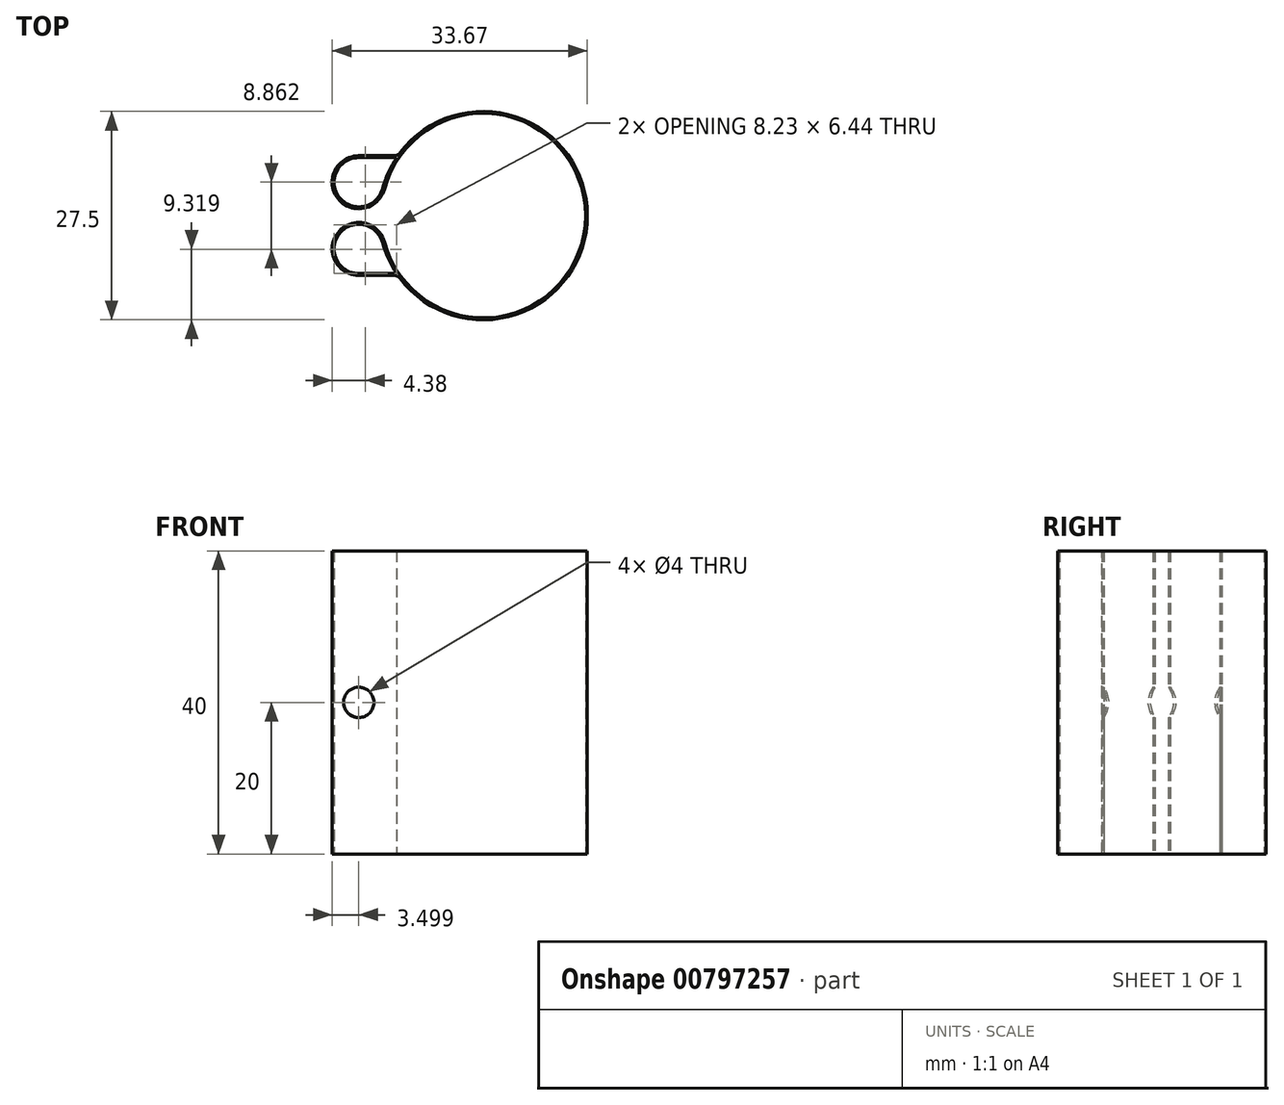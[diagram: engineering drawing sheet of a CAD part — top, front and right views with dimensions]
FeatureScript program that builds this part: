
annotation { "Feature Type Name" : "Feature", "Feature Type Description" : "" }
export const myFeature = defineFeature(function(context is Context, id is Id, definition is map)
    precondition{}
    {
        {
            var Q0;
            Q0=qCreatedBy(makeId("Top.planeOp"),FACE);
            var sketch = newSketch(context, id + "F0", { "sketchPlane" : qUnion([Q0])});
            skArc(sketch, "E0", {"start": v(-13.04, -3.5) * mm, "mid": v(13.5, 0) * mm, "end": v(-13.04, 3.5) * mm});
            skArc(sketch, "E1", {"start": v(-13.28, -3.56) * mm, "mid": v(-12.52, -5.68) * mm, "end": v(-11.43, -7.65) * mm});
            skLineSegment(sketch, "E2", {"start": v(0, 0) * mm, "end": v(13.75, 0) * mm, "construction": true});
            skLineSegment(sketch, "E3.1.0", {"start": v(0, 0) * mm, "end": v(0, 13.75) * mm, "construction": true});
            skLineSegment(sketch, "E3.2.0", {"start": v(0, 0) * mm, "end": v(-13.75, 0) * mm, "construction": true});
            skLineSegment(sketch, "E3.3.0", {"start": v(0, 0) * mm, "end": v(0, -13.75) * mm, "construction": true});
            skCircle(sketch, "E4", {"center": v(0, 0) * mm, "radius": 17 * mm, "construction": true});
            skLineSegment(sketch, "E5", {"start": v(0, 0) * mm, "end": v(-16.42, -4.4) * mm, "construction": true});
            skArc(sketch, "E6", {"start": v(-13.04, -3.5) * mm, "mid": v(-19.2, -2.27) * mm, "end": v(-16.42, -7.9) * mm});
            skArc(sketch, "E7", {"start": v(-13.28, -3.56) * mm, "mid": v(-19, -2.42) * mm, "end": v(-16.42, -7.65) * mm});
            skLineSegment(sketch, "E8", {"start": v(-16.42, -4.4) * mm, "end": v(-16.42, -7.9) * mm, "construction": true});
            skLineSegment(sketch, "E9", {"start": v(-16.42, -7.9) * mm, "end": v(-11.25, -7.9) * mm});
            skLineSegment(sketch, "E10", {"start": v(-16.42, -7.65) * mm, "end": v(-11.43, -7.65) * mm});
            skLineSegment(sketch, "E11.MirrorCS", {"start": v(-16.42, 4.4) * mm, "end": v(-16.42, 7.9) * mm, "construction": true});
            skLineSegment(sketch, "E12.MirrorCS", {"start": v(-16.42, 7.9) * mm, "end": v(-11.25, 7.9) * mm});
            skArc(sketch, "E13.MirrorC", {"start": v(-13.28, 3.56) * mm, "mid": v(-19, 2.42) * mm, "end": v(-16.42, 7.65) * mm});
            skLineSegment(sketch, "E14.MirrorCS", {"start": v(-16.42, 7.65) * mm, "end": v(-11.12, 7.65) * mm});
            skArc(sketch, "E15.MirrorC", {"start": v(-13.04, 3.5) * mm, "mid": v(-19.2, 2.27) * mm, "end": v(-16.42, 7.9) * mm});
            skLineSegment(sketch, "E16.MirrorCS", {"start": v(0, 0) * mm, "end": v(-16.42, 4.4) * mm, "construction": true});
            skArc(sketch, "E17.trimOffspring", {"start": v(-15.17, -7.67) * mm, "mid": v(-15.15, -7.66) * mm, "end": v(-15.12, -7.65) * mm});
            skPoint(sketch, "E18.orphan", {"position": v(-11.12, -7.65) * mm});
            skArc(sketch, "E19.trimOffspring", {"start": v(-11.25, -7.9) * mm, "mid": v(13.54, 2.4) * mm, "end": v(-13.28, 3.56) * mm});
            skArc(sketch, "E20.trimOffspring", {"start": v(-15.17, 7.67) * mm, "mid": v(-15.15, 7.66) * mm, "end": v(-15.12, 7.65) * mm});
            skSolve(sketch);
        }
        {
            var Q0;
            Q0 = qSketchRegion(id + "F0", true);
            extrude(context, id + "F1", {"entities" : qUnion([Q0]), "depth" : 40 * mm, "offsetDistance" : 25 * mm});
        }
        {
            var Q0;
            Q0=makeQuery(id+"F1.opExtrude","SWEPT_EDGE",EDGE,{"disambiguationData":[OSD([sQuery(id+"F0.wireOp",EDGE,"E12.MirrorCS"),sQuery(id+"F0.wireOp",EDGE,"E19.trimOffspring")])]});
            var Q1;
            Q1=makeQuery(id+"F1.opExtrude","SWEPT_EDGE",EDGE,{"disambiguationData":[OSD([sQuery(id+"F0.wireOp",EDGE,"E9"),sQuery(id+"F0.wireOp",EDGE,"E19.trimOffspring")])]});
            fillet(context, id + "F2", {"entities" : qUnion([Q0, Q1]), "radius" : 1 * mm, "tangentPropagation" : true, "allowEdgeOverflow" : false});
        }
        {
            var Q0;
            Q0=makeQuery(id+"F1.opExtrude","SWEPT_FACE",FACE,{"disambiguationData":[OSD([sQuery(id+"F0.wireOp",EDGE,"E12.MirrorCS")])]});
            var sketch = newSketch(context, id + "F3", { "sketchPlane" : qUnion([Q0])});
            skCircle(sketch, "E21", {"center": v(16.42, 20) * mm, "radius": 2 * mm});
            skSolve(sketch);
        }
        {
            var Q0;
            Q0 = qSketchRegion(id + "F3", true);
            extrude(context, id + "F4", {"entities" : qUnion([Q0]), "operationType" : NewBodyOperationType.REMOVE, "oppositeDirection" : true, "depth" : 25 * mm, "offsetDistance" : 25 * mm});
        }
    });
